# Revit family: 5LBS6030BSD25T,BSD45T
name_source: partatom
category: Plumbing Fixtures
revit_build: Autodesk Revit LT 2017 (Build: 20160225_1515(x64)
units: mm (PartAtom-declared; Revit-internal decimal feet)

## family parameters
Always vertical = Yes
Cut with Voids When Loaded = No
OmniClass Number = 23.45.05.14.17
OmniClass Title = Showers
Part Type = Normal
Room Calculation Point = No
Round Connector Dimension = Use Diameter
Shared = No
Work Plane-Based = No

## types (2) — shared parameters
Assembly Code = D2010710
Description = 4 x 8 Subway Tile, Traditional Threshold
Keynote = 22 40 00.B3
Manufacturer = Best Bath Systems, Inc.
Pan Void Height = 3/4"
Type Comments = Barrier Free
URL = http://www.bestbath.com
Unit Width = 60"

## per-type parameters (varying)
| type | Soap Ledge Height | Threshold Height | Unit Height |
| 5LBS6030BSD25T | 4 1/2" | 2 1/2" | 81" |
| 5LBS6030BSD45T | 6 1/2" | 4 1/2" | 83" |

note: column(s) folded — value = type name in every type: Model

## geometry (parser evidence)
native form markers: Sweep x2
no freeform markers — native parametric forms only
